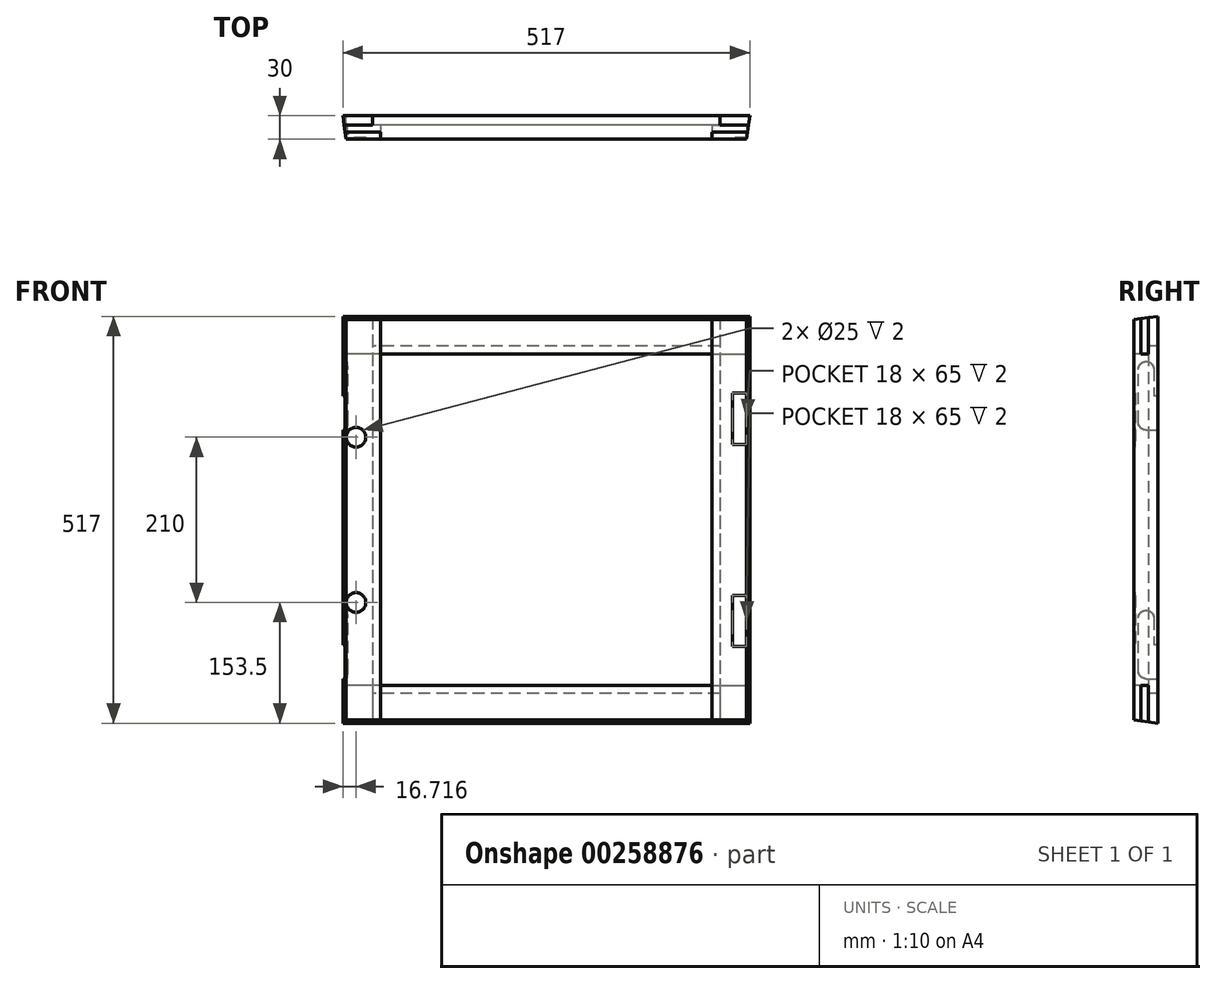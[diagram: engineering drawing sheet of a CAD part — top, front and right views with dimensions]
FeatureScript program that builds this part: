
annotation { "Feature Type Name" : "Feature", "Feature Type Description" : "" }
export const myFeature = defineFeature(function(context is Context, id is Id, definition is map)
    precondition{}
    {
        {
            assignVariable(context, id + "F0", {"name" : "Width", "anyValue" : 517});
        }
        {
            assignVariable(context, id + "F1", {"name" : "Height", "anyValue" : 517});
        }
        {
            var Q0;
            Q0=qCreatedBy(makeId("Top.planeOp"),FACE);
            var sketch = newSketch(context, id + "F2", { "sketchPlane" : qUnion([Q0])});
            skLineSegment(sketch, "E0", {"start": v(-254.28, -30) * mm, "end": v(-210.5, -30) * mm});
            skLineSegment(sketch, "E1", {"start": v(-210.5, -30) * mm, "end": v(-210.5, -12) * mm});
            skLineSegment(sketch, "E2", {"start": v(-210.5, -12) * mm, "end": v(-220.5, -12) * mm});
            skLineSegment(sketch, "E3", {"start": v(-220.5, -12) * mm, "end": v(-220.5, 0) * mm});
            skLineSegment(sketch, "E4", {"start": v(-220.5, 0) * mm, "end": v(-258.5, 0) * mm});
            skLineSegment(sketch, "E5", {"start": v(-258.5, 0) * mm, "end": v(-254.28, -30) * mm});
            skLineSegment(sketch, "E6", {"start": v(-254.28, -30) * mm, "end": v(-254.28, 53.54) * mm, "construction": true});
            skLineSegment(sketch, "E7.MirrorCS", {"start": v(210.5, -12) * mm, "end": v(220.5, -12) * mm});
            skLineSegment(sketch, "E8.MirrorCS", {"start": v(254.28, -30) * mm, "end": v(210.5, -30) * mm});
            skLineSegment(sketch, "E9.MirrorCS", {"start": v(258.5, 0) * mm, "end": v(254.28, -30) * mm});
            skLineSegment(sketch, "E10.MirrorCS", {"start": v(210.5, -30) * mm, "end": v(210.5, -12) * mm});
            skLineSegment(sketch, "E11.MirrorCS", {"start": v(220.5, 0) * mm, "end": v(258.5, 0) * mm});
            skLineSegment(sketch, "E12.MirrorCS", {"start": v(254.28, -30) * mm, "end": v(254.28, 53.54) * mm, "construction": true});
            skLineSegment(sketch, "E13.MirrorCS", {"start": v(220.5, -12) * mm, "end": v(220.5, 0) * mm});
            skSolve(sketch);
        }
        {
            var Q0;
            Q0 = qSketchRegion(id + "F2", true);
            extrude(context, id + "F3", {"entities" : qUnion([Q0]), "endBound" : BoundingType.SYMMETRIC, "depth" : (getVariable(context, 'Height')) * mm});
        }
        {
            var Q0;
            Q0=qCreatedBy(makeId("Right.planeOp"),FACE);
            var sketch = newSketch(context, id + "F4", { "sketchPlane" : qUnion([Q0])});
            skLineSegment(sketch, "E14", {"start": v(-30, 254.28) * mm, "end": v(-30, 210.5) * mm});
            skLineSegment(sketch, "E15", {"start": v(-30, 210.5) * mm, "end": v(-12, 210.5) * mm});
            skLineSegment(sketch, "E16", {"start": v(-12, 210.5) * mm, "end": v(-12, 220.5) * mm});
            skLineSegment(sketch, "E17", {"start": v(-12, 220.5) * mm, "end": v(0, 220.5) * mm});
            skLineSegment(sketch, "E18", {"start": v(0, 220.5) * mm, "end": v(0, 258.5) * mm});
            skLineSegment(sketch, "E19", {"start": v(0, 258.5) * mm, "end": v(-30, 254.28) * mm});
            skLineSegment(sketch, "E20", {"start": v(-30, 254.28) * mm, "end": v(60.96, 254.28) * mm, "construction": true});
            skLineSegment(sketch, "E21.MirrorCS", {"start": v(-12, -220.5) * mm, "end": v(0, -220.5) * mm});
            skLineSegment(sketch, "E22.MirrorCS", {"start": v(-12, -210.5) * mm, "end": v(-12, -220.5) * mm});
            skLineSegment(sketch, "E23.MirrorCS", {"start": v(0, -258.5) * mm, "end": v(-30, -254.28) * mm});
            skLineSegment(sketch, "E24.MirrorCS", {"start": v(0, -220.5) * mm, "end": v(0, -258.5) * mm});
            skLineSegment(sketch, "E25.MirrorCS", {"start": v(-30, -254.28) * mm, "end": v(60.96, -254.28) * mm, "construction": true});
            skLineSegment(sketch, "E26.MirrorCS", {"start": v(-30, -210.5) * mm, "end": v(-12, -210.5) * mm});
            skLineSegment(sketch, "E27.MirrorCS", {"start": v(-30, -254.28) * mm, "end": v(-30, -210.5) * mm});
            skSolve(sketch);
        }
        {
            var Q0;
            Q0 = qSketchRegion(id + "F4", true);
            var Q1;
            Q1=makeQuery(id+"Fvmf2te3hUVuNpQ_1.opExtrude","SWEPT_FACE",FACE,{"disambiguationData":[OSD([sQuery(id+"FzqBh2jlssyKnJa_1.wireOp",EDGE,"wrGozak8-ePD3-3w1G-4Yc4-uoNr4usTV6Cc")])]});
            var Q2;
            Q2=makeQuery(id+"F3.opExtrude","SWEPT_FACE",FACE,{"disambiguationData":[OSD([sQuery(id+"F2.wireOp",EDGE,"E5")])]});
            extrude(context, id + "F5", {"entities" : qUnion([Q0]), "endBound" : BoundingType.SYMMETRIC, "endBoundEntityFace" : qUnion([Q1]), "depth" : (getVariable(context, 'Width')) * mm});
        }
        {
            var Q0;
            Q0=qCreatedBy(makeId("Right.planeOp"),FACE);
            var sketch = newSketch(context, id + "F6", { "sketchPlane" : qUnion([Q0])});
            skLineSegment(sketch, "E28", {"start": v(24.47, -261.94) * mm, "end": v(-48.75, -251.65) * mm});
            skLineSegment(sketch, "E29", {"start": v(-48.75, -251.65) * mm, "end": v(-48.75, -295.9) * mm});
            skLineSegment(sketch, "E30", {"start": v(-48.75, -295.9) * mm, "end": v(0, -295.9) * mm});
            skLineSegment(sketch, "E31", {"start": v(0, -295.9) * mm, "end": v(24.47, -261.94) * mm});
            skLineSegment(sketch, "E32", {"start": v(25.9, 262.14) * mm, "end": v(-47.85, 251.77) * mm});
            skLineSegment(sketch, "E33", {"start": v(-47.85, 251.77) * mm, "end": v(-47.85, 276.14) * mm});
            skLineSegment(sketch, "E34", {"start": v(-47.85, 276.14) * mm, "end": v(26.37, 270.36) * mm});
            skLineSegment(sketch, "E35", {"start": v(26.37, 270.36) * mm, "end": v(25.9, 262.14) * mm});
            skSolve(sketch);
        }
        {
            var Q0;
            Q0 = qSketchRegion(id + "F6", true);
            extrude(context, id + "F7", {"entities" : qUnion([Q0]), "operationType" : NewBodyOperationType.REMOVE, "endBound" : BoundingType.THROUGH_ALL, "oppositeDirection" : true, "depth" : 25 * mm, "hasSecondDirection" : true, "secondDirectionBound" : SecondDirectionBoundingType.THROUGH_ALL, "secondDirectionOppositeDirection" : false, "secondDirectionDepth" : 25 * mm});
        }
        {
            var Q0;
            Q0=qCreatedBy(makeId("Top.planeOp"),FACE);
            var sketch = newSketch(context, id + "F8", { "sketchPlane" : qUnion([Q0])});
            skLineSegment(sketch, "E36", {"start": v(251.42, -50.39) * mm, "end": v(260.46, 13.97) * mm});
            skLineSegment(sketch, "E37", {"start": v(260.46, 13.97) * mm, "end": v(300.2, 13.97) * mm});
            skLineSegment(sketch, "E38", {"start": v(300.2, 13.97) * mm, "end": v(300.2, -48.7) * mm});
            skLineSegment(sketch, "E39", {"start": v(300.2, -48.7) * mm, "end": v(251.42, -50.39) * mm});
            skLineSegment(sketch, "E40", {"start": v(-251.62, -48.96) * mm, "end": v(-261.57, 21.88) * mm});
            skLineSegment(sketch, "E41", {"start": v(-261.57, 21.88) * mm, "end": v(-297.83, 21.88) * mm});
            skLineSegment(sketch, "E42", {"start": v(-297.83, 21.88) * mm, "end": v(-297.83, -49.2) * mm});
            skLineSegment(sketch, "E43", {"start": v(-297.83, -49.2) * mm, "end": v(-251.62, -48.96) * mm});
            skSolve(sketch);
        }
        {
            var Q0;
            Q0 = qSketchRegion(id + "F8", true);
            extrude(context, id + "F9", {"entities" : qUnion([Q0]), "operationType" : NewBodyOperationType.REMOVE, "endBound" : BoundingType.THROUGH_ALL, "oppositeDirection" : true, "depth" : 25 * mm, "hasSecondDirection" : true, "secondDirectionBound" : SecondDirectionBoundingType.THROUGH_ALL, "secondDirectionOppositeDirection" : false, "secondDirectionDepth" : 25 * mm});
        }
        {
            var Q0;
            Q0=makeQuery(id+"F3.opExtrude","SWEPT_FACE",FACE,{"disambiguationData":[OSD([sQuery(id+"F2.wireOp",EDGE,"E5")])]});
            var sketch = newSketch(context, id + "F10", { "sketchPlane" : qUnion([Q0])});
            skLineSegment(sketch, "E44", {"start": v(-20.98, 545.94) * mm, "end": v(-20.98, -3.93) * mm, "construction": true});
            skArc(sketch, "E45", {"start": v(-10.98, 191.06) * mm, "mid": v(-20.98, 201.06) * mm, "end": v(-30.98, 191.06) * mm});
            skLineSegment(sketch, "E46", {"start": v(-10.98, 124.06) * mm, "end": v(-10.98, 191.06) * mm});
            skLineSegment(sketch, "E47", {"start": v(-30.98, 191.06) * mm, "end": v(-30.98, 157.06) * mm});
            skLineSegment(sketch, "E48", {"start": v(-20.98, 114.06) * mm, "end": v(-35.98, 114.06) * mm});
            skLineSegment(sketch, "E49", {"start": v(-35.98, 114.06) * mm, "end": v(-35.98, 157.06) * mm});
            skLineSegment(sketch, "E50", {"start": v(-35.98, 157.06) * mm, "end": v(-30.98, 157.06) * mm});
            skLineSegment(sketch, "E51.0.1.0", {"start": v(-30.98, -124.94) * mm, "end": v(-30.98, -158.94) * mm});
            skLineSegment(sketch, "E51.0.1.1", {"start": v(-20.98, -201.94) * mm, "end": v(-35.98, -201.94) * mm});
            skLineSegment(sketch, "E51.0.1.2", {"start": v(-35.98, -201.94) * mm, "end": v(-35.98, -158.94) * mm});
            skArc(sketch, "E51.0.1.4", {"start": v(-10.98, -124.94) * mm, "mid": v(-20.98, -114.94) * mm, "end": v(-30.98, -124.94) * mm});
            skLineSegment(sketch, "E51.0.1.5", {"start": v(-10.98, -191.94) * mm, "end": v(-10.98, -124.94) * mm});
            skLineSegment(sketch, "E51.0.1.6", {"start": v(-35.98, -158.94) * mm, "end": v(-30.98, -158.94) * mm});
            skLineSegment(sketch, "E51.direction1", {"start": v(-35.98, 114.06) * mm, "end": v(-11.53, 114.06) * mm, "construction": true});
            skLineSegment(sketch, "E51.direction2", {"start": v(-35.98, 114.06) * mm, "end": v(-35.98, -201.94) * mm, "construction": true});
            skArc(sketch, "E52", {"start": v(-20.98, -201.94) * mm, "mid": v(-13.9, -199.01) * mm, "end": v(-10.98, -191.94) * mm});
            skArc(sketch, "E53", {"start": v(-20.98, 114.06) * mm, "mid": v(-13.9, 116.99) * mm, "end": v(-10.98, 124.06) * mm});
            skSolve(sketch);
        }
        {
            var Q0;
            Q0 = qSketchRegion(id + "F10", true);
            extrude(context, id + "F11", {"entities" : qUnion([Q0]), "operationType" : NewBodyOperationType.REMOVE, "oppositeDirection" : true, "depth" : 3 * mm});
        }
        {
            var Q0;
            Q0=makeQuery(id+"F3.opExtrude","SWEPT_FACE",FACE,{"disambiguationData":[OSD([sQuery(id+"F2.wireOp",EDGE,"E8.MirrorCS")])]});
            var sketch = newSketch(context, id + "F12", { "sketchPlane" : qUnion([Q0])});
            skLineSegment(sketch, "E54.bottom", {"start": v(254.28, -161) * mm, "end": v(236.28, -161) * mm});
            skLineSegment(sketch, "E54.top", {"start": v(254.28, -96) * mm, "end": v(236.28, -96) * mm});
            skLineSegment(sketch, "E54.left", {"start": v(254.28, -161) * mm, "end": v(254.28, -96) * mm});
            skLineSegment(sketch, "E54.right", {"start": v(236.28, -161) * mm, "end": v(236.28, -96) * mm});
            skLineSegment(sketch, "E55.bottom", {"start": v(254.28, 96) * mm, "end": v(236.28, 96) * mm});
            skLineSegment(sketch, "E55.top", {"start": v(254.28, 161) * mm, "end": v(236.28, 161) * mm});
            skLineSegment(sketch, "E55.left", {"start": v(254.28, 96) * mm, "end": v(254.28, 161) * mm});
            skLineSegment(sketch, "E55.right", {"start": v(236.28, 96) * mm, "end": v(236.28, 161) * mm});
            skSolve(sketch);
        }
        {
            var Q0;
            Q0 = qSketchRegion(id + "F12", true);
            extrude(context, id + "F13", {"entities" : qUnion([Q0]), "operationType" : NewBodyOperationType.REMOVE, "oppositeDirection" : true, "depth" : 2 * mm});
        }
        {
            var Q0;
            Q0=makeQuery(id+"F3.opExtrude","SWEPT_FACE",FACE,{"disambiguationData":[OSD([sQuery(id+"F2.wireOp",EDGE,"E0")])]});
            var sketch = newSketch(context, id + "F14", { "sketchPlane" : qUnion([Q0])});
            skCircle(sketch, "E56", {"center": v(-241.78, 105) * mm, "radius": 12.5 * mm});
            skCircle(sketch, "E57", {"center": v(-241.78, -105) * mm, "radius": 12.5 * mm});
            skSolve(sketch);
        }
        {
            var Q0;
            Q0 = qSketchRegion(id + "F14", true);
            extrude(context, id + "F15", {"entities" : qUnion([Q0]), "operationType" : NewBodyOperationType.REMOVE, "oppositeDirection" : true, "depth" : 2 * mm});
        }
        {
            var Q0;
            Q0=makeQuery(id+"F3.opExtrude","SWEPT_FACE",FACE,{"disambiguationData":[OSD([sQuery(id+"F2.wireOp",EDGE,"E8.MirrorCS")])]});
            var Q1;
            Q1=makeQuery(id+"F3.opExtrude","SWEPT_FACE",FACE,{"disambiguationData":[OSD([sQuery(id+"F2.wireOp",EDGE,"E11.MirrorCS")])]});
            cPlane(context, id + "F16", {"entities" : qUnion([Q0, Q1]), "cplaneType" : CPlaneType.MID_PLANE, "offset" : 25 * mm, "width" : 150 * mm, "height" : 150 * mm});
        }
        {
            var Q0;
            Q0=qCreatedBy(id+"F16.planeOp",FACE);
            var sketch = newSketch(context, id + "F17", { "sketchPlane" : qUnion([Q0])});
            skLineSegment(sketch, "E58.bottom", {"start": v(210.5, -269.58) * mm, "end": v(275.32, -269.58) * mm});
            skLineSegment(sketch, "E58.top", {"start": v(210.5, -210.5) * mm, "end": v(275.32, -210.5) * mm});
            skLineSegment(sketch, "E58.left", {"start": v(210.5, -269.58) * mm, "end": v(210.5, -210.5) * mm});
            skLineSegment(sketch, "E58.right", {"start": v(275.32, -269.58) * mm, "end": v(275.32, -210.5) * mm});
            skLineSegment(sketch, "E59.0", {"start": v(258.5, -210.5) * mm, "end": v(-258.5, -210.5) * mm, "construction": true});
            skLineSegment(sketch, "E60.0", {"start": v(210.5, 254.28) * mm, "end": v(210.5, -254.28) * mm, "construction": true});
            skSolve(sketch);
        }
        {
            var Q0;
            Q0 = qSketchRegion(id + "F17", true);
            extrude(context, id + "F18", {"entities" : qUnion([Q0]), "oppositeDirection" : true, "depth" : 3 * mm, "hasSecondDirection" : true, "secondDirectionOppositeDirection" : false, "secondDirectionDepth" : 6 * mm});
        }
        {
            var Q0;
            Q0=makeQuery(id+"F18.opExtrude","SWEPT_BODY",BODY,{"disambiguationData":[OSD([sQuery(id+"F17.wireOp",EDGE,"E58.bottom"),sQuery(id+"F17.wireOp",EDGE,"E58.top"),sQuery(id+"F17.wireOp",EDGE,"E58.left"),sQuery(id+"F17.wireOp",EDGE,"E58.right")])]});
            var Q1;
            Q1=qCreatedBy(makeId("Top.planeOp"),FACE);
            mirror(context, id + "F19", {"entities" : qUnion([Q0]), "mirrorPlane" : qUnion([Q1])});
        }
        {
            var Q0;
            Q0=makeQuery(id+"F18.opExtrude","SWEPT_BODY",BODY,{"disambiguationData":[OSD([sQuery(id+"F17.wireOp",EDGE,"E58.bottom"),sQuery(id+"F17.wireOp",EDGE,"E58.top"),sQuery(id+"F17.wireOp",EDGE,"E58.left"),sQuery(id+"F17.wireOp",EDGE,"E58.right")])]});
            var Q1;
            Q1=makeQuery(id+"F19.opPattern","COPY",BODY,{"derivedFrom":makeQuery(id+"F18.opExtrude","SWEPT_BODY",BODY,{"disambiguationData":[OSD([sQuery(id+"F17.wireOp",EDGE,"E58.bottom"),sQuery(id+"F17.wireOp",EDGE,"E58.top"),sQuery(id+"F17.wireOp",EDGE,"E58.left"),sQuery(id+"F17.wireOp",EDGE,"E58.right")])]}),"instanceName":"1"});
            var Q2;
            Q2=qCreatedBy(makeId("Right.planeOp"),FACE);
            mirror(context, id + "F20", {"entities" : qUnion([Q0, Q1]), "mirrorPlane" : qUnion([Q2])});
        }
        {
            var Q0;
            Q0=makeQuery(id+"F18.opExtrude","SWEPT_BODY",BODY,{"disambiguationData":[OSD([sQuery(id+"F17.wireOp",EDGE,"E58.bottom"),sQuery(id+"F17.wireOp",EDGE,"E58.top"),sQuery(id+"F17.wireOp",EDGE,"E58.left"),sQuery(id+"F17.wireOp",EDGE,"E58.right")])]});
            var Q1;
            Q1=makeQuery(id+"F19.opPattern","COPY",BODY,{"derivedFrom":makeQuery(id+"F18.opExtrude","SWEPT_BODY",BODY,{"disambiguationData":[OSD([sQuery(id+"F17.wireOp",EDGE,"E58.bottom"),sQuery(id+"F17.wireOp",EDGE,"E58.top"),sQuery(id+"F17.wireOp",EDGE,"E58.left"),sQuery(id+"F17.wireOp",EDGE,"E58.right")])]}),"instanceName":"1"});
            var Q2;
            Q2=makeQuery(id+"F20.opPattern","COPY",BODY,{"derivedFrom":makeQuery(id+"F19.opPattern","COPY",BODY,{"derivedFrom":makeQuery(id+"F18.opExtrude","SWEPT_BODY",BODY,{"disambiguationData":[OSD([sQuery(id+"F17.wireOp",EDGE,"E58.bottom"),sQuery(id+"F17.wireOp",EDGE,"E58.top"),sQuery(id+"F17.wireOp",EDGE,"E58.left"),sQuery(id+"F17.wireOp",EDGE,"E58.right")])]}),"instanceName":"1"}),"instanceName":"1"});
            var Q3;
            Q3=makeQuery(id+"F20.opPattern","COPY",BODY,{"derivedFrom":makeQuery(id+"F18.opExtrude","SWEPT_BODY",BODY,{"disambiguationData":[OSD([sQuery(id+"F17.wireOp",EDGE,"E58.bottom"),sQuery(id+"F17.wireOp",EDGE,"E58.top"),sQuery(id+"F17.wireOp",EDGE,"E58.left"),sQuery(id+"F17.wireOp",EDGE,"E58.right")])]}),"instanceName":"1"});
            var Q4;
            Q4=makeQuery(id+"F3.opExtrude","SWEPT_BODY",BODY,{"disambiguationData":[OSD([sQuery(id+"F2.wireOp",EDGE,"E7.MirrorCS"),sQuery(id+"F2.wireOp",EDGE,"E8.MirrorCS"),sQuery(id+"F2.wireOp",EDGE,"E9.MirrorCS"),sQuery(id+"F2.wireOp",EDGE,"E10.MirrorCS"),sQuery(id+"F2.wireOp",EDGE,"E11.MirrorCS"),sQuery(id+"F2.wireOp",EDGE,"E13.MirrorCS")])]});
            var Q5;
            Q5=makeQuery(id+"F3.opExtrude","SWEPT_BODY",BODY,{"disambiguationData":[OSD([sQuery(id+"F2.wireOp",EDGE,"E0"),sQuery(id+"F2.wireOp",EDGE,"E1"),sQuery(id+"F2.wireOp",EDGE,"E2"),sQuery(id+"F2.wireOp",EDGE,"E3"),sQuery(id+"F2.wireOp",EDGE,"E4"),sQuery(id+"F2.wireOp",EDGE,"E5")])]});
            booleanBodies(context, id + "F21", {"operationType" : BooleanOperationType.SUBTRACTION, "tools" : qUnion([Q0, Q1, Q2, Q3]), "targets" : qUnion([Q4, Q5])});
        }
        {
            var Q0;
            Q0=makeQuery(id+"F3.opExtrude","SWEPT_BODY",BODY,{"disambiguationData":[OSD([sQuery(id+"F2.wireOp",EDGE,"E7.MirrorCS"),sQuery(id+"F2.wireOp",EDGE,"E8.MirrorCS"),sQuery(id+"F2.wireOp",EDGE,"E9.MirrorCS"),sQuery(id+"F2.wireOp",EDGE,"E10.MirrorCS"),sQuery(id+"F2.wireOp",EDGE,"E11.MirrorCS"),sQuery(id+"F2.wireOp",EDGE,"E13.MirrorCS")])]});
            var Q1;
            Q1=makeQuery(id+"F3.opExtrude","SWEPT_BODY",BODY,{"disambiguationData":[OSD([sQuery(id+"F2.wireOp",EDGE,"E0"),sQuery(id+"F2.wireOp",EDGE,"E1"),sQuery(id+"F2.wireOp",EDGE,"E2"),sQuery(id+"F2.wireOp",EDGE,"E3"),sQuery(id+"F2.wireOp",EDGE,"E4"),sQuery(id+"F2.wireOp",EDGE,"E5")])]});
            var Q2;
            Q2=makeQuery(id+"F5.opExtrude","SWEPT_BODY",BODY,{"disambiguationData":[OSD([sQuery(id+"F4.wireOp",EDGE,"E21.MirrorCS"),sQuery(id+"F4.wireOp",EDGE,"E22.MirrorCS"),sQuery(id+"F4.wireOp",EDGE,"E23.MirrorCS"),sQuery(id+"F4.wireOp",EDGE,"E24.MirrorCS"),sQuery(id+"F4.wireOp",EDGE,"E26.MirrorCS"),sQuery(id+"F4.wireOp",EDGE,"E27.MirrorCS")])]});
            var Q3;
            Q3=makeQuery(id+"F5.opExtrude","SWEPT_BODY",BODY,{"disambiguationData":[OSD([sQuery(id+"F4.wireOp",EDGE,"E14"),sQuery(id+"F4.wireOp",EDGE,"E15"),sQuery(id+"F4.wireOp",EDGE,"E16"),sQuery(id+"F4.wireOp",EDGE,"E17"),sQuery(id+"F4.wireOp",EDGE,"E18"),sQuery(id+"F4.wireOp",EDGE,"E19")])]});
            booleanBodies(context, id + "F22", {"operationType" : BooleanOperationType.SUBTRACTION, "tools" : qUnion([Q0, Q1]), "targets" : qUnion([Q2, Q3]), "keepTools" : true});
        }
    });
